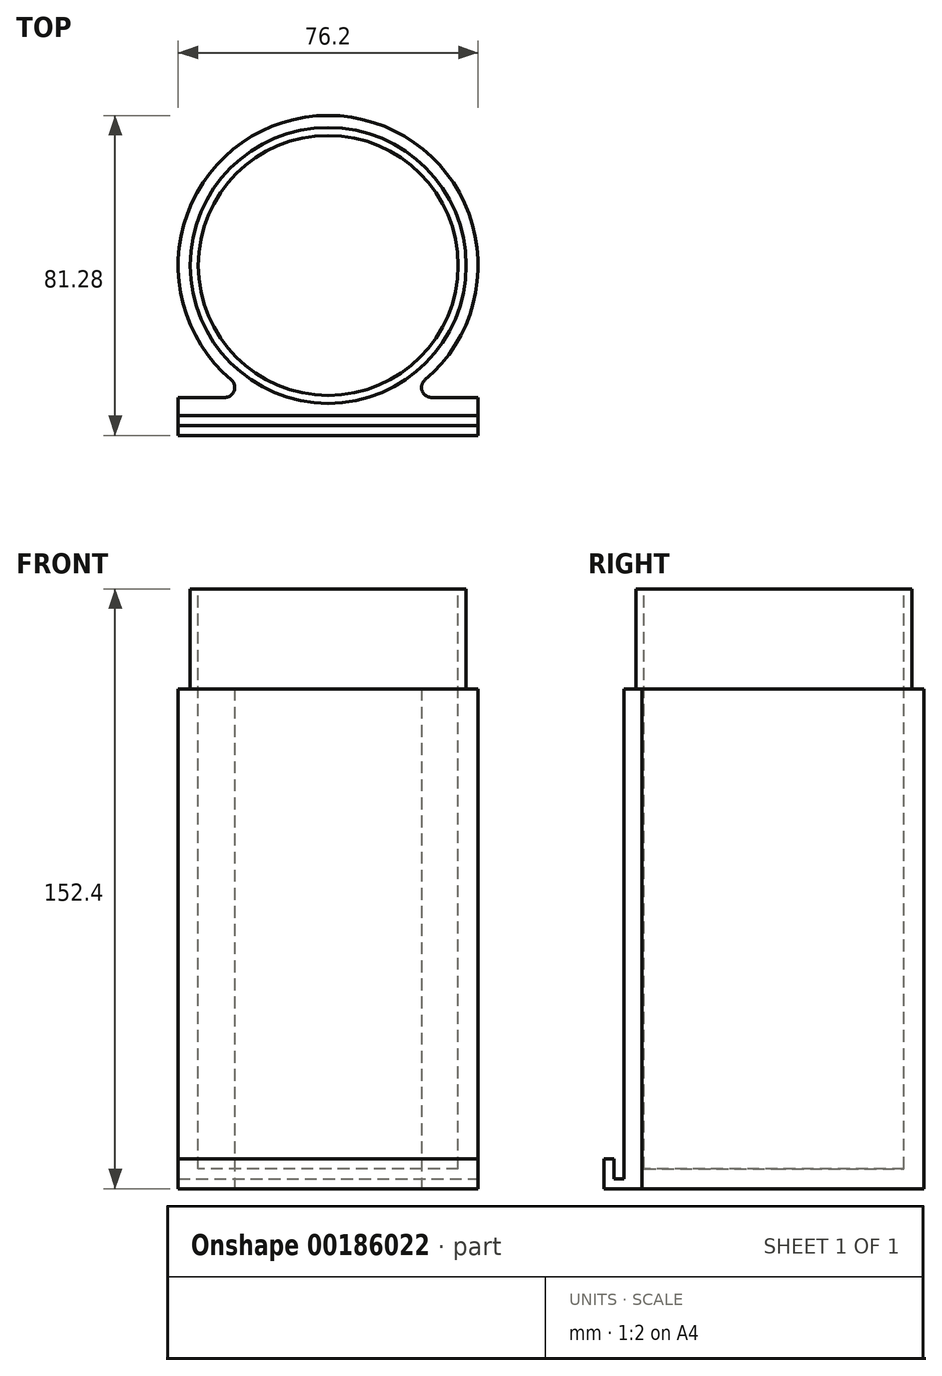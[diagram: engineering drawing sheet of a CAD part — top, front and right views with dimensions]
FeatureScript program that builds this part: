
annotation { "Feature Type Name" : "Feature", "Feature Type Description" : "" }
export const myFeature = defineFeature(function(context is Context, id is Id, definition is map)
    precondition{}
    {
        {
            var Q0;
            Q0=qCreatedBy(makeId("Top.planeOp"),FACE);
            var sketch = newSketch(context, id + "F0", { "sketchPlane" : qUnion([Q0])});
            skCircle(sketch, "E0", {"center": v(0, 0) * mm, "radius": 38.1 * mm, "construction": true});
            skLineSegment(sketch, "E1.bottom", {"start": v(-38.1, -38.1) * mm, "end": v(38.1, -38.1) * mm, "construction": true});
            skLineSegment(sketch, "E1.top", {"start": v(-38.1, -33.55) * mm, "end": v(38.1, -33.55) * mm, "construction": true});
            skLineSegment(sketch, "E1.left", {"start": v(-38.1, -38.1) * mm, "end": v(-38.1, -33.55) * mm, "construction": true});
            skLineSegment(sketch, "E1.right", {"start": v(38.1, -38.1) * mm, "end": v(38.1, -33.55) * mm, "construction": true});
            skArc(sketch, "E2", {"start": v(18.05, -33.55) * mm, "mid": v(0, 38.1) * mm, "end": v(-18.05, -33.55) * mm});
            skLineSegment(sketch, "E3", {"start": v(-18.05, -33.55) * mm, "end": v(-38.1, -33.55) * mm});
            skLineSegment(sketch, "E4", {"start": v(-38.1, -38.1) * mm, "end": v(38.1, -38.1) * mm});
            skLineSegment(sketch, "E5", {"start": v(38.1, -33.55) * mm, "end": v(18.05, -33.55) * mm});
            skLineSegment(sketch, "E6", {"start": v(-38.1, -38.1) * mm, "end": v(-38.1, -33.55) * mm});
            skLineSegment(sketch, "E7", {"start": v(38.1, -38.1) * mm, "end": v(38.1, -33.55) * mm});
            skSolve(sketch);
        }
        {
            var Q0;
            Q0=makeQuery(id+"F0.imprint","IMPRINT",FACE,{"disambiguationData":[TD([[makeQuery(id+"F0.imprint","IMPRINT",EDGE,{"derivedFrom":sQuery(id+"F0.wireOp",EDGE,"E2")}),1.0]])]});
            extrude(context, id + "F1", {"entities" : qUnion([Q0]), "depth" : 127 * mm});
        }
        {
            var Q0;
            Q0=makeQuery(id+"F1.opExtrude","CAP_FACE",FACE,{"disambiguationData":[OSD([sQuery(id+"F0.wireOp",EDGE,"E2"),sQuery(id+"F0.wireOp",EDGE,"E3"),sQuery(id+"F0.wireOp",EDGE,"E4"),sQuery(id+"F0.wireOp",EDGE,"E5"),sQuery(id+"F0.wireOp",EDGE,"E6"),sQuery(id+"F0.wireOp",EDGE,"E7")])],"isStart":false});
            var sketch = newSketch(context, id + "F2", { "sketchPlane" : qUnion([Q0])});
            skCircle(sketch, "E8", {"center": v(0, 0) * mm, "radius": 33.02 * mm});
            skCircle(sketch, "E9", {"center": v(0, 0) * mm, "radius": 35.05 * mm});
            skSolve(sketch);
        }
        {
            var Q0;
            Q0=makeQuery(id+"F2.imprint","IMPRINT",FACE,{"disambiguationData":[TD([[makeQuery(id+"F2.imprint","IMPRINT",EDGE,{"derivedFrom":sQuery(id+"F2.wireOp",EDGE,"E8")}),1.0]])]});
            extrude(context, id + "F3", {"entities" : qUnion([Q0]), "operationType" : NewBodyOperationType.REMOVE, "oppositeDirection" : true, "depth" : 121.92 * mm});
        }
        {
            var Q0;
            Q0 = qSketchRegion(id + "F2", true);
            extrude(context, id + "F4", {"entities" : qUnion([Q0]), "operationType" : NewBodyOperationType.ADD, "depth" : 25.4 * mm});
        }
        {
            var Q0;
            Q0=makeQuery(id+"F1.opExtrude","SWEPT_EDGE",EDGE,{"disambiguationData":[OSD([sQuery(id+"F0.wireOp",EDGE,"E2"),sQuery(id+"F0.wireOp",EDGE,"E5")])]});
            var Q1;
            Q1=makeQuery(id+"F1.opExtrude","SWEPT_EDGE",EDGE,{"disambiguationData":[OSD([sQuery(id+"F0.wireOp",EDGE,"E2"),sQuery(id+"F0.wireOp",EDGE,"E3")])]});
            fillet(context, id + "F5", {"entities" : qUnion([Q0, Q1]), "radius" : 2.54 * mm, "tangentPropagation" : true, "allowEdgeOverflow" : false});
        }
        {
            var Q0;
            Q0=makeQuery(id+"F1.opExtrude","SWEPT_FACE",FACE,{"disambiguationData":[OSD([sQuery(id+"F0.wireOp",EDGE,"E4")])]});
            var sketch = newSketch(context, id + "F6", { "sketchPlane" : qUnion([Q0])});
            skLineSegment(sketch, "E10.bottom", {"start": v(-38.1, 0) * mm, "end": v(38.1, 0) * mm});
            skLineSegment(sketch, "E10.top", {"start": v(-38.1, 2.54) * mm, "end": v(38.1, 2.54) * mm});
            skLineSegment(sketch, "E10.left", {"start": v(-38.1, 0) * mm, "end": v(-38.1, 2.54) * mm});
            skLineSegment(sketch, "E10.right", {"start": v(38.1, 0) * mm, "end": v(38.1, 2.54) * mm});
            skSolve(sketch);
        }
        {
            var Q0;
            Q0=makeQuery(id+"F6.imprint","IMPRINT",FACE,{"disambiguationData":[TD([[makeQuery(id+"F6.imprint","IMPRINT",EDGE,{"derivedFrom":sQuery(id+"F6.wireOp",EDGE,"E10.bottom")}),1.0]])]});
            extrude(context, id + "F7", {"entities" : qUnion([Q0]), "operationType" : NewBodyOperationType.ADD, "depth" : 5.08 * mm});
        }
        {
            var Q0;
            Q0=makeQuery(id+"F7.opExtrude","SWEPT_FACE",FACE,{"disambiguationData":[OSD([sQuery(id+"F6.wireOp",EDGE,"E10.top")])]});
            var sketch = newSketch(context, id + "F8", { "sketchPlane" : qUnion([Q0])});
            skLineSegment(sketch, "E11.bottom", {"start": v(-38.1, -43.18) * mm, "end": v(38.1, -43.18) * mm});
            skLineSegment(sketch, "E11.top", {"start": v(-38.1, -40.64) * mm, "end": v(38.1, -40.64) * mm});
            skLineSegment(sketch, "E11.left", {"start": v(-38.1, -43.18) * mm, "end": v(-38.1, -40.64) * mm});
            skLineSegment(sketch, "E11.right", {"start": v(38.1, -43.18) * mm, "end": v(38.1, -40.64) * mm});
            skSolve(sketch);
        }
        {
            var Q0;
            Q0=makeQuery(id+"F8.imprint","IMPRINT",FACE,{"disambiguationData":[TD([[makeQuery(id+"F8.imprint","IMPRINT",EDGE,{"derivedFrom":sQuery(id+"F8.wireOp",EDGE,"E11.bottom")}),1.0]])]});
            extrude(context, id + "F9", {"entities" : qUnion([Q0]), "operationType" : NewBodyOperationType.ADD, "depth" : 5.08 * mm});
        }
    });
